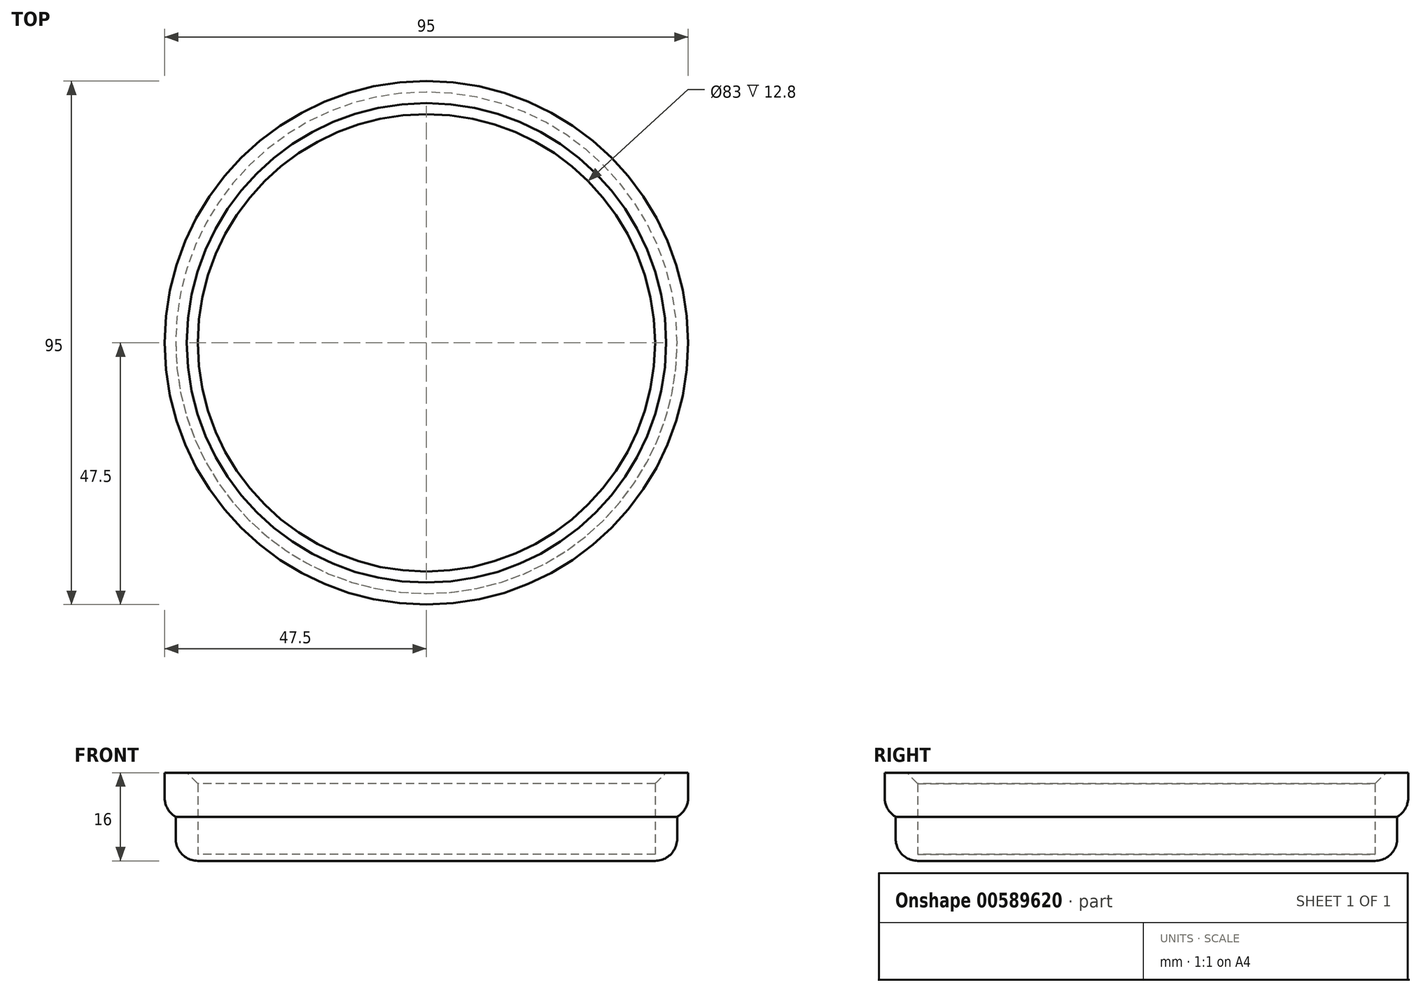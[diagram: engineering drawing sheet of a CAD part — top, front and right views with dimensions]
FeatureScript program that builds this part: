
annotation { "Feature Type Name" : "Feature", "Feature Type Description" : "" }
export const myFeature = defineFeature(function(context is Context, id is Id, definition is map)
    precondition{}
    {
        {
            var Q0;
            Q0=qCreatedBy(makeId("Top.planeOp"),FACE);
            var sketch = newSketch(context, id + "F0", { "sketchPlane" : qUnion([Q0])});
            skCircle(sketch, "E0", {"center": v(0, 0) * mm, "radius": 47.5 * mm});
            skCircle(sketch, "E1", {"center": v(0, 0) * mm, "radius": 41.5 * mm});
            skSolve(sketch);
        }
        {
            var Q0;
            Q0=makeQuery(id+"F0.imprint","IMPRINT",FACE,{"disambiguationData":[TD([[makeQuery(id+"F0.imprint","IMPRINT",EDGE,{"derivedFrom":sQuery(id+"F0.wireOp",EDGE,"E0")}),1.0]])]});
            extrude(context, id + "F1", {"entities" : qUnion([Q0]), "depth" : 16 * mm, "offsetDistance" : 25 * mm});
        }
        {
            var Q0;
            Q0=makeQuery(id+"F0.imprint","IMPRINT",FACE,{"disambiguationData":[TD([[makeQuery(id+"F0.imprint","IMPRINT",EDGE,{"derivedFrom":sQuery(id+"F0.wireOp",EDGE,"E1")}),1.0]])]});
            extrude(context, id + "F2", {"entities" : qUnion([Q0]), "operationType" : NewBodyOperationType.ADD, "depth" : 1.2 * mm, "offsetDistance" : 25 * mm});
        }
        {
            var Q0;
            Q0=makeQuery(id+"F1.opExtrude","CAP_EDGE",EDGE,{"disambiguationData":[OSD([sQuery(id+"F0.wireOp",EDGE,"E1")])],"isStart":false});
            chamfer(context, id + "F3", {"entities" : qUnion([Q0]), "width" : 2 * mm, "tangentPropagation" : true});
        }
        {
            var Q0;
            {var subQ0=sQuery(id+"F0.wireOp",EDGE,"E1");Q0=makeQuery(id+"F2.boolean.opBoolean","MERGE",FACE,{"derivedFrom":[makeQuery(id+"F1.opExtrude","CAP_FACE",FACE,{"disambiguationData":[OSD([sQuery(id+"F0.wireOp",EDGE,"E0"),subQ0])],"isStart":true}),makeQuery(id+"F2.opExtrude","CAP_FACE",FACE,{"disambiguationData":[OSD([subQ0])],"isStart":true})]});}
            var sketch = newSketch(context, id + "F4", { "sketchPlane" : qUnion([Q0])});
            skCircle(sketch, "E2", {"center": v(0, 0) * mm, "radius": 45.5 * mm});
            skCircle(sketch, "E3", {"center": v(0, 0) * mm, "radius": 48.44 * mm});
            skSolve(sketch);
        }
        {
            var Q0;
            Q0=makeQuery(id+"F4.imprint","IMPRINT",FACE,{"disambiguationData":[TD([[makeQuery(id+"F4.imprint","IMPRINT",EDGE,{"derivedFrom":sQuery(id+"F4.wireOp",EDGE,"E3")}),1.0]])]});
            var Q1;
            Q1=makeQuery(id+"F4.imprint","IMPRINT",FACE,{"disambiguationData":[TD([[makeQuery(id+"F4.imprint","IMPRINT",EDGE,{"derivedFrom":sQuery(id+"F4.wireOp",EDGE,"E2")}),-1.0]])]});
            var Q2;
            Q2=sQuery(id+"F4.wireOp",EDGE,"E2");
            var Q3;
            Q3=sQuery(id+"F4.wireOp",EDGE,"E3");
            extrude(context, id + "F5", {"entities" : qUnion([Q0, Q1]), "operationType" : NewBodyOperationType.REMOVE, "surfaceEntities" : qUnion([Q2, Q3]), "endBound" : BoundingType.SYMMETRIC, "oppositeDirection" : true, "depth" : 16 * mm, "offsetDistance" : 25 * mm});
        }
        {
            var Q0;
            Q0=makeQuery(id+"F5.boolean.opBoolean","INTERSECT",EDGE,{"derivedFrom":[makeQuery(id+"F1.opExtrude","SWEPT_FACE",FACE,{"disambiguationData":[OSD([sQuery(id+"F0.wireOp",EDGE,"E0")])]}),makeQuery(id+"F5.opExtrude","CAP_FACE",FACE,{"disambiguationData":[OSD([sQuery(id+"F4.wireOp",EDGE,"E2"),sQuery(id+"F4.wireOp",EDGE,"E3")])],"isStart":false})]});
            var Q1;
            {var subQ0=sQuery(id+"F0.wireOp",EDGE,"E1");Q1=makeQuery(id+"F5.boolean.opBoolean","INTERSECT",EDGE,{"derivedFrom":[makeQuery(id+"F2.boolean.opBoolean","MERGE",FACE,{"derivedFrom":[makeQuery(id+"F1.opExtrude","CAP_FACE",FACE,{"disambiguationData":[OSD([sQuery(id+"F0.wireOp",EDGE,"E0"),subQ0])],"isStart":true}),makeQuery(id+"F2.opExtrude","CAP_FACE",FACE,{"disambiguationData":[OSD([subQ0])],"isStart":true})]}),makeQuery(id+"F5.opExtrude","SWEPT_FACE",FACE,{"disambiguationData":[OSD([sQuery(id+"F4.wireOp",EDGE,"E2")])]})]});}
            fillet(context, id + "F6", {"entities" : qUnion([Q0, Q1]), "radius" : 4 * mm, "tangentPropagation" : true, "allowEdgeOverflow" : false});
        }
    });
